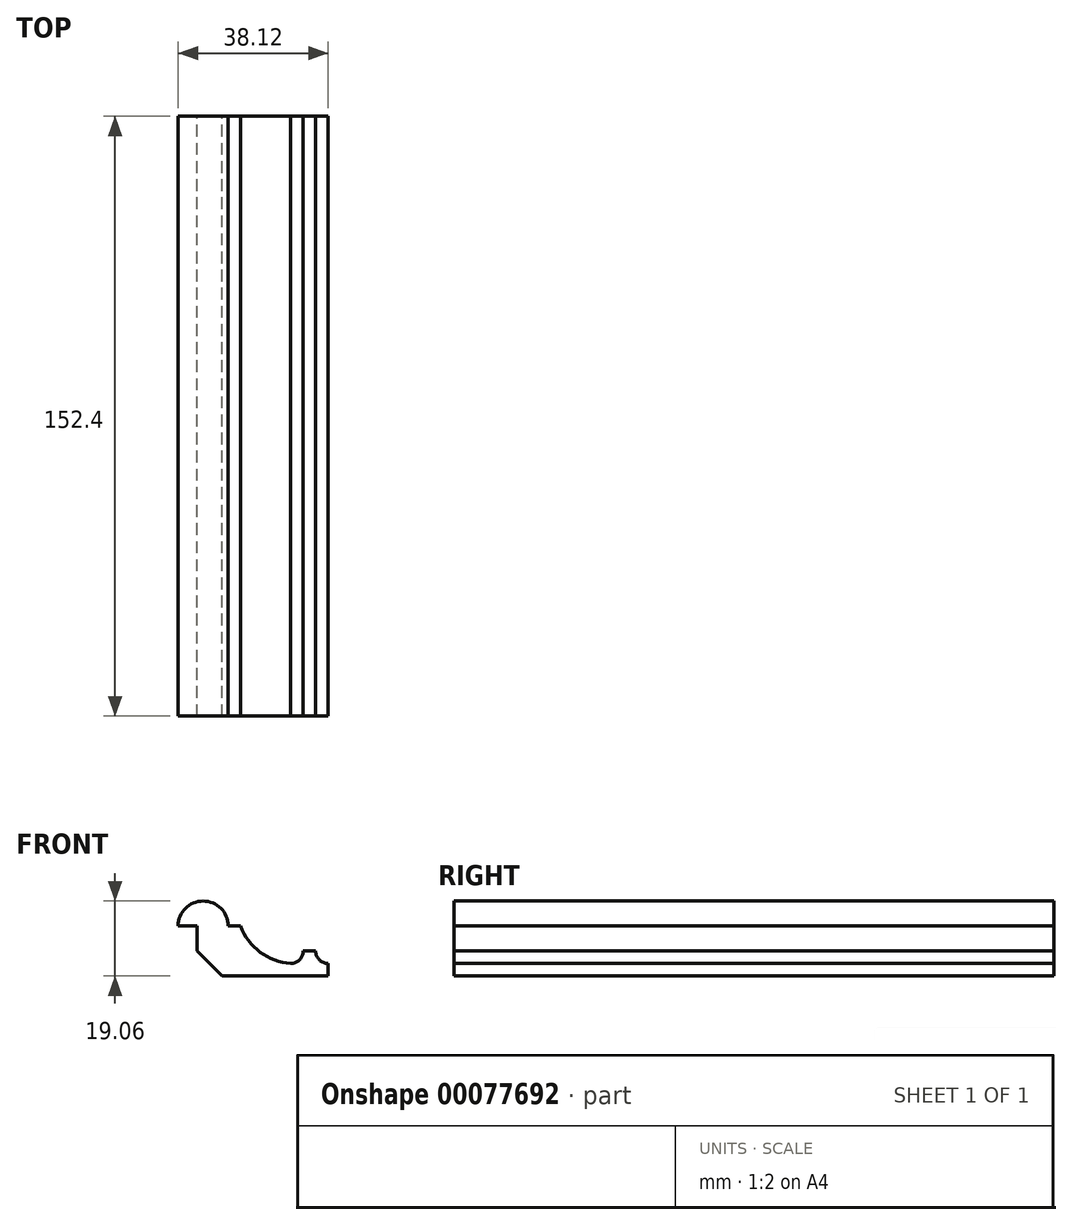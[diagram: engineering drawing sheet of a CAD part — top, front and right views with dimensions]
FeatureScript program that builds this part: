
annotation { "Feature Type Name" : "Feature", "Feature Type Description" : "" }
export const myFeature = defineFeature(function(context is Context, id is Id, definition is map)
    precondition{}
    {
        {
            var Q0;
            Q0=qCreatedBy(makeId("Front.planeOp"),FACE);
            var sketch = newSketch(context, id + "F0", { "sketchPlane" : qUnion([Q0])});
            skArc(sketch, "E0", {"start": v(-12.7, 9.53) * mm, "mid": v(-17.2, 7.67) * mm, "end": v(-19.06, 3.18) * mm});
            skArc(sketch, "E1", {"start": v(-6.35, 3.18) * mm, "mid": v(-8.21, 7.67) * mm, "end": v(-12.7, 9.53) * mm});
            skLineSegment(sketch, "E2", {"start": v(-19.06, 3.18) * mm, "end": v(-14.3, 3.18) * mm});
            skLineSegment(sketch, "E3", {"start": v(-14.3, 3.18) * mm, "end": v(-14.3, -3.18) * mm});
            skLineSegment(sketch, "E4", {"start": v(-14.3, -3.18) * mm, "end": v(-7.94, -9.53) * mm});
            skLineSegment(sketch, "E5", {"start": v(-7.94, -9.53) * mm, "end": v(19.06, -9.53) * mm});
            skLineSegment(sketch, "E6", {"start": v(19.06, -9.53) * mm, "end": v(19.06, -6.35) * mm});
            skLineSegment(sketch, "E7", {"start": v(15.88, -3.18) * mm, "end": v(12.7, -3.18) * mm});
            skLineSegment(sketch, "E8", {"start": v(-6.35, 3.18) * mm, "end": v(-3.18, 3.18) * mm});
            skArc(sketch, "E9", {"start": v(15.88, -3.18) * mm, "mid": v(16.81, -5.42) * mm, "end": v(19.06, -6.35) * mm});
            skArc(sketch, "E10", {"start": v(9.53, -6.35) * mm, "mid": v(11.78, -5.42) * mm, "end": v(12.7, -3.18) * mm});
            skArc(sketch, "E11", {"start": v(-3.18, 3.18) * mm, "mid": v(1.77, -3.46) * mm, "end": v(9.53, -6.35) * mm});
            skSolve(sketch);
        }
        {
            var Q0;
            Q0=makeQuery(id+"F0.imprint","IMPRINT",FACE,{"disambiguationData":[TD([[makeQuery(id+"F0.imprint","IMPRINT",EDGE,{"derivedFrom":sQuery(id+"F0.wireOp",EDGE,"E0")}),1.0]])]});
            extrude(context, id + "F1", {"entities" : qUnion([Q0]), "depth" : 152.4 * mm});
        }
    });
